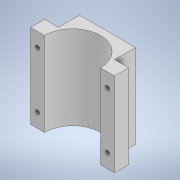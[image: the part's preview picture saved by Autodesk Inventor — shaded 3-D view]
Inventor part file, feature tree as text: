
AUTODESK INVENTOR PART (.ipt)
format: ipt  version: 2021.2 (Build 252289000, 289)  size: 482,304 bytes
history: native  units: in
note: dims shown in document units (in); Inventor stores cm internally (conversion verified against a paired STEP export)
features: sketch x5, extrude x3, hole x2
ambient origin geometry x8: Origin, YZ Plane, XZ Plane, XY Plane, X Axis, Y Axis, Z Axis, Center Point
bodies: Solid2 (feature_tree)
feature tree (10):
  extrude  "Extrusion9"  Depth=0.25in
  hole  "Hole3"  [1 undecoded]
  hole  "Hole4"  [1 undecoded]
  extrude  "Extrusion10"  Depth=0.5in
  extrude  "Extrusion11"  Depth=0.5in
  sketch  "Sketch18"  dims[d78=2.0in d79=0.25in]
  sketch  "Sketch19"  dims[d80=0.5in d81=3.0in]
  sketch  "Sketch20"  dims[d82=0.0in d83=0.25in]
  sketch  "Sketch21"  dims[d84=0.25in d85=0.5in]
  sketch  "Sketch22"  dims[d86=0.5in d87=0.15in d88=0.75in d89=0.191in d90=0.219in d91=0.5635in d92=0.0625in d93=0.0in d94=0.5in d95=0.5in d96=1.0in d97=1.0in d98=0.186in d99=0.75in d100=0.204in d101=0.219in d102=0.5635in d103=0.0625in d104=0.0in d105=0.75in d106=0.5in d107=0.75in d108=0.0in d109=0.0in d110=1.0in d111=2.0in d112=0.05in d113=0.0in]
note: 2 required parameter values undecoded (feature->parameter linkage not recoverable at this tier; creation-order binding heuristic only, values carry confidence <= 0.55)
